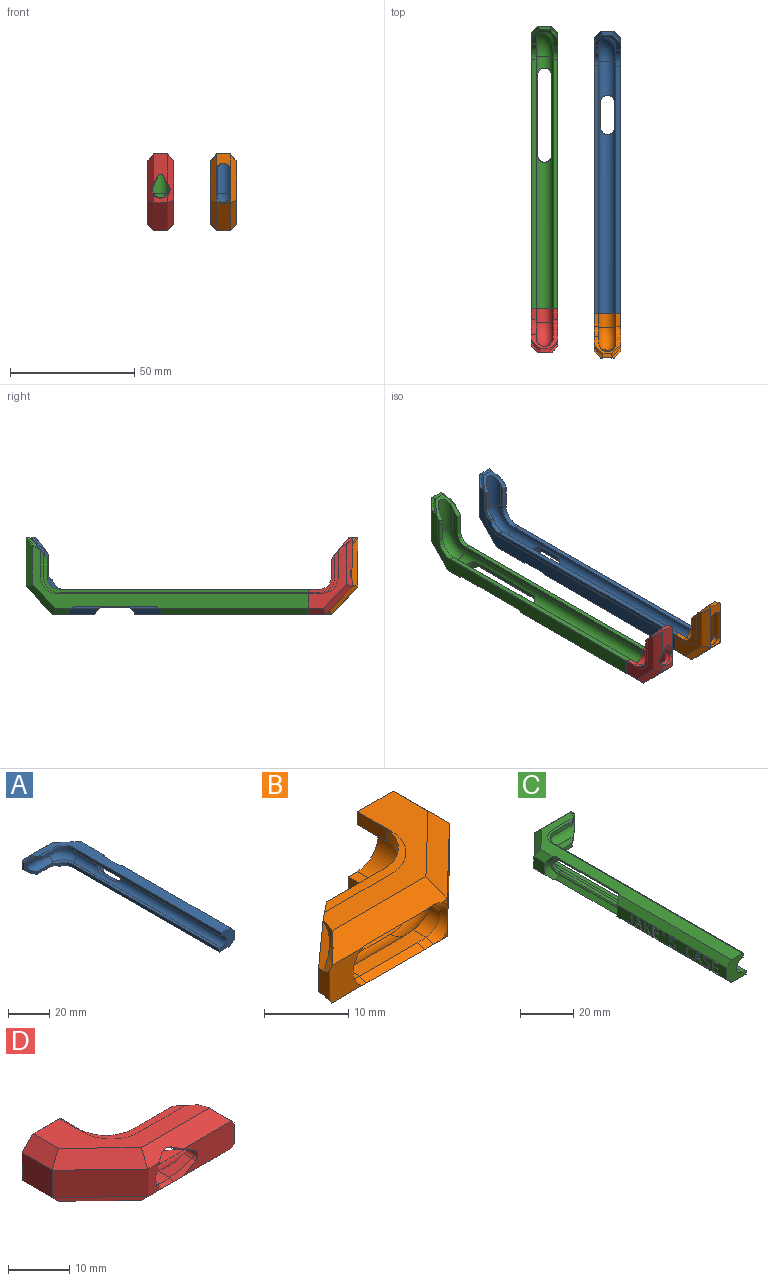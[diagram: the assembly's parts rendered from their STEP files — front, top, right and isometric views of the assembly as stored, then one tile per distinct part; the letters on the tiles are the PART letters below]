
ASSEMBLY  parts=4 mates=2
PART A: 59 faces, bbox 45.8x131.7x47.1 mm
  f0: plane 10.75x7.07mm, normal (-0.63,-0.78,0), area 27.3mm2, adj f1,f5,f6,f7,f8,f9,f15,f27
  f1: plane 107.74x17.21mm, normal (0,0,-1), area 24.9mm2, adj f0,f31,f32,f44,f52,f53,f54,f55
  f2: plane 15.59x6.28mm, normal (1,0,0), area 78.9mm2, adj f3,f19,f22,f23
  f3: plane 11.22x10.82mm, normal (0.69,0.72,0), area 84.7mm2, adj f2,f4,f18,f24
  f4: plane 19.84x5.44mm, normal (0,1,0), area 107.9mm2, adj f3,f7,f16,f17,f25
  f5: cylinder r=0.51mm len=8.54mm, axis (1,0,0), area 7mm2, adj f0,f9,f13,f28
  f6: plane 4.34x3.96mm, normal (-0.56,0,-0.83), area 4.9mm2, adj f0,f7,f26
  f7: plane 5.4x1.58mm, normal (-1,0,0), area 7.5mm2, adj f0,f4,f6,f8,f16,f25,f26
  f8: plane 4.39x4.01mm, normal (-0.56,0,0.83), area 5.1mm2, adj f0,f7,f16
  f9: plane 7.84x1.24mm, normal (0,-1,0), area 9.7mm2, adj f0,f5,f30,f31
  f10: cylinder r=0.51mm len=10.2mm, axis (0,-1,0), area 12.1mm2, adj f12,f14,f21,f33
  f11: cylinder r=0.51mm len=10.2mm, axis (0,-1,0), area 12.3mm2, adj f12,f14,f20,f35
  f12: bspline ~7.32x3.94mm, area 9.9mm2, adj f10,f11,f22,f36
  f13: bspline ~3.96x1.52mm, area 1.8mm2, adj f5,f29,f30,f39
  f14: bspline ~7.32x3.93mm, area 9.9mm2, adj f10,f11,f34,f41
  f15: bspline ~23.11x23.11mm, area 0.1mm2, adj f0,f16,f51
  f16: bspline ~23.11x23.11mm, area 5.8mm2, adj f4,f7,f8,f15,f17,f51
  f17: plane 19.78x2.54mm, normal (0,0.71,0.71), area 63mm2, adj f4,f16,f18,f51
  f18: plane 12.24x11.9mm, normal (0.49,0.51,0.71), area 52.2mm2, adj f3,f17,f19,f51
  f19: plane 16.98x3.13mm, normal (0.71,0,0.71), area 53.1mm2, adj f2,f18,f22,f51
  f20: plane 10.2x1.56mm, normal (0.72,0,-0.7), area 22.1mm2, adj f11,f22,f41,f51
  f21: plane 10.2x1.73mm, normal (0.69,0,0.73), area 24.3mm2, adj f10,f22,f41,f50
  f22: bspline ~16.25x7.94mm, area 45.7mm2, adj f2,f12,f19,f20,f21,f23,f50,f51
  f23: plane 17.36x3.2mm, normal (0.71,0,-0.71), area 53.6mm2, adj f2,f22,f24,f50
  f24: plane 12.24x11.9mm, normal (0.49,0.51,-0.71), area 52.2mm2, adj f3,f23,f25,f50
  f25: plane 19.84x2.54mm, normal (0,0.71,-0.71), area 63.3mm2, adj f4,f7,f24,f26,f50
  f26: bspline ~23.11x23.11mm, area 5.3mm2, adj f6,f7,f25,f27,f50
  f27: bspline ~23.11x23.11mm, area 0mm2, adj f0,f26,f28,f50
  f28: plane 8.54x0.06mm, normal (0,-0.99,-0.12), area 0.5mm2, adj f5,f27,f29,f50
  f29: bspline ~6.39x2.18mm, area 0.1mm2, adj f13,f28,f38,f50
  f30: cylinder r=4.1mm len=3.88mm, axis (0,0,1), area 6.4mm2, adj f9,f13,f31,f39,f40,f45
  f31: cylinder r=3.43mm len=15.1mm, axis (1,0,0), area 145.4mm2, adj f0,f1,f9,f30,f32,f45
  f32: torus R=6.37mm, axis (0,0,-1), area 144.5mm2, adj f1,f31,f44,f45
  f33: plane 10.2x1.33mm, normal (0,0,1), area 13.6mm2, adj f10,f34,f36,f44
  f34: cylinder r=2.79mm len=5.59mm, axis (-1,0,0), area 11.4mm2, adj f14,f33,f35,f44
  f35: plane 10.2x1.39mm, normal (0,0,-1), area 14.2mm2, adj f11,f34,f36,f44
  f36: cylinder r=2.79mm len=5.59mm, axis (-1,0,0), area 11.4mm2, adj f12,f33,f35,f44
  f37: cylinder r=6.37mm len=6.37mm, axis (0,0,-1), area 0.2mm2, adj f38,f43,f46,f50
  f38: plane 0.87x0.02mm, normal (0,-1,0), area 0mm2, adj f29,f37,f43,f50
  f39: torus R=4.61mm, axis (0,0,-1), area 2.7mm2, adj f13,f30,f40,f43
  f40: cylinder r=4.77mm len=5.29mm, axis (0,0,1), area 12.9mm2, adj f30,f39,f42,f43,f45
  f41: bspline ~16.25x7.94mm, area 45.7mm2, adj f14,f20,f21,f47,f48,f49,f50,f51
  f42: plane 99.7x1.78mm, normal (-1,0,0), area 177.3mm2, adj f40,f43,f45,f52
  f43: plane 107.74x7.25mm, normal (0,0,-1), area 174.7mm2, adj f37,f38,f39,f40,f42,f46,f52
  f44: cylinder r=3.43mm len=101.37mm, axis (0,-1,0), area 1024mm2, adj f1,f32,f33,f34,f35,f36,f45,f52
  f45: plane 107.74x8.86mm, normal (0,0,1), area 176.7mm2, adj f30,f31,f32,f40,f42,f44,f52
  f46: plane 101.37x0.02mm, normal (-1,0,0), area 2.1mm2, adj f37,f43,f50,f52
  f47: plane 74.13x3.14mm, normal (0.71,0,0.71), area 260.3mm2, adj f41,f49,f51,f52
  f48: plane 74.51x3.2mm, normal (0.71,0,-0.71), area 260.8mm2, adj f41,f49,f50,f52
  f49: plane 72.74x6.29mm, normal (1,0,0), area 389.6mm2, adj f41,f47,f48,f52
  f50: plane 111.22x25.47mm, normal (0,0,-1), area 681.3mm2, adj f21,f22,f23,f24,f25,f26,f27,f28
  f51: plane 111.34x25.52mm, normal (0,0,1), area 682.3mm2, adj f15,f16,f17,f18,f19,f20,f22,f41
  f52: plane 10.52x10.11mm, normal (0,-1,0), area 68mm2, adj f1,f42,f43,f44,f45,f46,f47,f48
  f53: plane 99.61x1.87mm, normal (-1,0,0), area 186mm2, adj f1,f52,f55,f57,f58
  f54: plane 6.88x1.88mm, normal (0,-1,0), area 12.8mm2, adj f1,f55,f56,f58
  f55: cylinder r=6.27mm len=6.94mm, axis (0,0,1), area 20.9mm2, adj f1,f53,f54,f58
  f56: plane 1.89x1.88mm, normal (0,-1,0), area 3.5mm2, adj f0,f1,f54,f58
  f57: bspline ~0.09x0.04mm, area 0mm2, adj f52,f53,f58
  f58: plane 107.74x17.22mm, normal (0,0,1), area 25mm2, adj f0,f51,f53,f54,f55,f56,f57
PART B: 51 faces, bbox 39.8x36x47.2 mm
  f0: plane 17.45x11.89mm, normal (0,0,-1), area 22.2mm2, adj f13,f16,f17,f18,f44,f45,f46,f47
  f1: plane 25.55x15.24mm, normal (0,0,1), area 116.6mm2, adj f33,f35,f39,f40,f43,f44,f50
  f2: plane 5.7x5.46mm, normal (0,-1,0), area 24.1mm2, adj f7,f12,f34,f35,f42,f43
  f3: plane 1.07x0.98mm, normal (0,-1,0), area 0.4mm2, adj f5,f31,f43
  f4: plane 25.54x15.19mm, normal (0,0,-1), area 116.7mm2, adj f7,f8,f9,f10,f11,f37,f38,f42
  f5: plane 12.21x11.81mm, normal (0.69,-0.72,0), area 83.4mm2, adj f3,f31,f36,f38,f40,f41
  f6: plane 9.77x1.02mm, normal (0,-0.45,0.89), area 11.2mm2, adj f21,f32,f34,f42
  f7: bspline ~23.11x23.11mm, area 5.6mm2, adj f2,f4,f8,f12,f27,f42
  f8: bspline ~23.11x23.11mm, area 0.1mm2, adj f4,f7,f9,f13
  f9: plane 11.08x0.02mm, normal (0,1,0), area 0.2mm2, adj f4,f8,f10,f19
  f10: cylinder r=6.37mm len=6.37mm, axis (0,0,-1), area 0.2mm2, adj f4,f9,f11,f19
  f11: plane 5.52x0.02mm, normal (-1,0,0), area 0.1mm2, adj f4,f10,f19,f44
  f12: plane 4.13x1.79mm, normal (-1,0,0), area 6.5mm2, adj f2,f7,f13,f27,f28,f35
  f13: plane 10.5x8.54mm, normal (-0.63,0.78,0), area 32.4mm2, adj f0,f8,f12,f15,f16,f19,f24,f27
  f14: cylinder r=4.73mm len=1.78mm, axis (0,0,-1), area 1.5mm2, adj f15,f19,f24,f25
  f15: plane 17.45x11.89mm, normal (0,0,1), area 54.1mm2, adj f13,f14,f16,f17,f18,f24,f25,f26
  f16: cylinder r=3.43mm len=15.36mm, axis (-1,0,0), area 89.5mm2, adj f0,f13,f15,f17,f20,f21,f23
  f17: torus R=6.37mm, axis (0,0,-1), area 127.5mm2, adj f0,f15,f16,f18,f21,f22,f23
  f18: cylinder r=3.43mm len=6.85mm, axis (0,-1,0), area 59.4mm2, adj f0,f15,f17,f44
  f19: plane 17.45x11.89mm, normal (0,0,-1), area 54.1mm2, adj f9,f10,f11,f13,f14,f24,f25,f26
  f20: cylinder r=2.32mm len=4.65mm, axis (0,1,0), area 15.6mm2, adj f16,f21,f23,f34
  f21: plane 11.25x2.27mm, normal (0,0,1), area 24.1mm2, adj f6,f16,f17,f20,f22,f32
  f22: cylinder r=2.32mm len=4.65mm, axis (0,1,0), area 15.8mm2, adj f17,f21,f23,f31
  f23: plane 11.25x2.26mm, normal (0,0,-1), area 24.1mm2, adj f16,f17,f20,f22,f29,f30
  f24: plane 7.58x1.78mm, normal (0,1,0), area 13.5mm2, adj f13,f14,f15,f19
  f25: cylinder r=4.79mm len=4.14mm, axis (0,0,1), area 11mm2, adj f14,f15,f19,f26
  f26: plane 4.87x1.78mm, normal (-1,0,0), area 8.7mm2, adj f15,f19,f25,f44
  f27: plane 3.88x3.76mm, normal (-0.67,0,-0.75), area 5.7mm2, adj f7,f12,f13
  f28: plane 3.9x3.79mm, normal (-0.67,0,0.75), area 5.8mm2, adj f12,f13,f35
  f29: plane 9.77x1.07mm, normal (0,-0.45,-0.9), area 11.7mm2, adj f23,f30,f34,f43
  f30: cone r=11.03mm half-angle=63.5deg, axis (0,0,1), area 1.9mm2, adj f23,f29,f31,f43
  f31: bspline ~10.32x6.08mm, area 11.6mm2, adj f3,f5,f22,f30,f32,f41,f42,f43
  f32: cone r=11.02mm half-angle=63.4deg, axis (0,0,-1), area 1.8mm2, adj f6,f21,f31,f42
  f33: bspline ~23.11x23.11mm, area 0.2mm2, adj f1,f13,f35
  f34: bspline ~10.32x6.9mm, area 7.2mm2, adj f2,f6,f20,f29,f42,f43
  f35: bspline ~23.11x23.11mm, area 6mm2, adj f1,f2,f12,f28,f33,f43
  f36: plane 6.91x5.44mm, normal (1,0,0), area 37.5mm2, adj f5,f37,f39,f44
  f37: plane 6.91x2.54mm, normal (0.71,0,-0.71), area 22.9mm2, adj f4,f36,f38,f44
  f38: plane 12.24x11.9mm, normal (0.49,-0.51,-0.71), area 52.2mm2, adj f4,f5,f37,f42
  f39: plane 6.91x2.54mm, normal (0.71,0,0.71), area 22.9mm2, adj f1,f36,f40,f44
  f40: plane 12.24x11.9mm, normal (0.49,-0.51,0.71), area 52.2mm2, adj f1,f5,f39,f43
  f41: plane 0.9x0.89mm, normal (0,-1,0), area 0.3mm2, adj f5,f31,f42
  f42: plane 19.45x2.62mm, normal (0,-0.71,-0.71), area 60mm2, adj f2,f4,f6,f7,f31,f32,f34,f38
  f43: plane 19.35x2.61mm, normal (0,-0.71,0.71), area 60.8mm2, adj f1,f2,f3,f29,f30,f31,f34,f35
  f44: plane 10.52x10.11mm, normal (0,1,0), area 68mm2, adj f0,f1,f4,f11,f15,f18,f19,f26
  f45: plane 6.93x1.87mm, normal (0,1,0), area 12.9mm2, adj f0,f46,f48,f50
  f46: cylinder r=6.29mm len=6.93mm, axis (0,0,1), area 18.5mm2, adj f0,f45,f47,f50
  f47: plane 4.96x1.87mm, normal (-1,0,0), area 9.3mm2, adj f0,f44,f46,f49,f50
  f48: plane 1.87x1.87mm, normal (0,1,0), area 3.5mm2, adj f0,f13,f45,f50
  f49: bspline ~0.09x0.04mm, area 0mm2, adj f44,f47,f50
  f50: plane 17.45x11.9mm, normal (0,0,1), area 22.2mm2, adj f1,f13,f45,f46,f47,f48,f49
PART C: 203 faces, bbox 45.8x131.7x47.1 mm
  f0: plane 107.74x17.21mm, normal (0,0,-1), area 41.8mm2, adj f1,f2,f9,f28,f37,f197,f198,f199
  f1: plane 10.5x8.65mm, normal (0.63,-0.78,0), area 35.3mm2, adj f0,f7,f8,f24,f26,f28,f39,f41
  f2: plane 10.52x10.21mm, normal (0,-1,0), area 68.5mm2, adj f0,f3,f4,f5,f6,f7,f8,f9
  f3: plane 11.84x5.47mm, normal (-1,0,0), area 47.1mm2, adj f2,f4,f5,f64,f65,f66,f67,f68
  f4: plane 61.01x3.15mm, normal (-0.71,0,0.71), area 212.9mm2, adj f2,f3,f6,f13,f14,f15,f22,f54
  f5: plane 61.1x3.18mm, normal (-0.71,0,-0.71), area 212.6mm2, adj f2,f3,f12,f13,f14,f15,f16,f17
  f6: plane 111.3x25.48mm, normal (0,0,1), area 667mm2, adj f2,f4,f19,f21,f22,f23,f24,f48
  f7: plane 107.74x17.21mm, normal (0,0,-1), area 209.3mm2, adj f1,f2,f10,f11,f38,f39,f40,f44
  f8: plane 107.74x17.21mm, normal (0,0,1), area 209.3mm2, adj f1,f2,f9,f10,f28,f37,f38,f39
  f9: cylinder r=3.43mm len=101.37mm, axis (0,1,0), area 879.2mm2, adj f0,f2,f8,f29,f30,f31,f32,f37
  f10: plane 100.21x1.78mm, normal (1,0,0), area 178.2mm2, adj f2,f7,f8,f38
  f11: plane 101.37x0.02mm, normal (1,0,0), area 2.1mm2, adj f2,f7,f12,f45
  f12: plane 111.27x25.52mm, normal (0,0,-1), area 670.3mm2, adj f2,f5,f11,f21,f22,f27,f43,f44
  f13: plane 11.2x5.47mm, normal (-1,0,0), area 33.3mm2, adj f4,f5,f54,f55,f56,f57,f58,f59
  f14: plane 31.59x6.32mm, normal (-1,0,0), area 117.6mm2, adj f4,f5,f22,f90,f91,f92,f93,f94
  f15: plane 10.36x5.51mm, normal (-1,0,0), area 38mm2, adj f4,f5,f85,f86,f87,f88,f100,f101
  f16: plane 2.88x1.67mm, normal (-1,0,0), area 3.9mm2, adj f5,f185,f191,f192
  f17: plane 2.88x1.67mm, normal (-1,0,0), area 3.9mm2, adj f5,f171,f177,f178
  f18: plane 2.57x2.17mm, normal (-1,0,0), area 3.4mm2, adj f5,f153,f164,f165
  f19: bspline ~23.11x23.11mm, area 5.8mm2, adj f6,f24,f26,f42,f47,f50
  f20: plane 11.22x10.82mm, normal (-0.69,0.72,0), area 84.7mm2, adj f25,f47,f49,f52
  f21: bspline ~16.27x7.89mm, area 45.8mm2, adj f6,f12,f23,f25,f34,f46,f48,f51
  f22: bspline ~16.27x7.89mm, area 45.8mm2, adj f4,f5,f6,f12,f14,f23,f36,f46
  f23: plane 32.32x1.6mm, normal (-0.71,0,-0.7), area 73mm2, adj f6,f21,f22,f33
  f24: bspline ~23.11x23.11mm, area 0.1mm2, adj f1,f6,f19
  f25: plane 6.68x6.28mm, normal (-1,0,0), area 30.6mm2, adj f20,f21,f48,f51
  f26: plane 5.4x1.58mm, normal (1,0,0), area 7.5mm2, adj f1,f19,f27,f41,f42,f47,f53
  f27: bspline ~23.11x23.11mm, area 5.3mm2, adj f12,f26,f41,f43,f53
  f28: cylinder r=3.43mm len=15.1mm, axis (1,0,0), area 145.7mm2, adj f0,f1,f8,f37
  f29: cylinder r=2.8mm len=5.59mm, axis (1,0,0), area 11.4mm2, adj f9,f30,f32,f34
  f30: plane 32.32x1.37mm, normal (0,0,-1), area 44.2mm2, adj f9,f29,f31,f33
  f31: cylinder r=2.8mm len=5.59mm, axis (1,0,0), area 11.4mm2, adj f9,f30,f32,f36
  f32: plane 32.32x1.35mm, normal (0,0,1), area 43.6mm2, adj f9,f29,f31,f35
  f33: cylinder r=0.51mm len=32.32mm, axis (0,1,0), area 38.7mm2, adj f23,f30,f34,f36
  f34: bspline ~7.33x3.93mm, area 9.9mm2, adj f21,f29,f33,f35
  f35: cylinder r=0.51mm len=32.32mm, axis (0,1,0), area 38.5mm2, adj f32,f34,f36,f46
  f36: bspline ~7.33x3.94mm, area 9.9mm2, adj f22,f31,f33,f35
  f37: torus R=6.37mm, axis (0,0,-1), area 144.5mm2, adj f0,f8,f9,f28
  f38: cylinder r=4.76mm len=4.13mm, axis (0,0,-1), area 8.9mm2, adj f7,f8,f10,f40
  f39: plane 7.39x1.78mm, normal (0,-1,0), area 13.1mm2, adj f1,f7,f8,f40
  f40: cylinder r=4.73mm len=2.44mm, axis (0,0,1), area 4.6mm2, adj f7,f8,f38,f39
  f41: plane 4.34x3.96mm, normal (0.56,0,-0.83), area 4.9mm2, adj f1,f26,f27
  f42: plane 4.39x4.01mm, normal (0.56,0,0.83), area 5.1mm2, adj f1,f19,f26
  f43: bspline ~23.11x23.11mm, area 0mm2, adj f1,f12,f27,f44
  f44: plane 10.84x0.02mm, normal (0,-1,0), area 0.2mm2, adj f7,f12,f43,f45
  f45: cylinder r=6.37mm len=6.37mm, axis (0,0,-1), area 0.2mm2, adj f7,f11,f12,f44
  f46: plane 32.32x1.63mm, normal (-0.7,0,0.72), area 73.5mm2, adj f12,f21,f22,f35
  f47: plane 19.84x5.44mm, normal (0,1,0), area 107.9mm2, adj f19,f20,f26,f50,f53
  f48: plane 8.23x3.16mm, normal (-0.71,0,0.71), area 21.4mm2, adj f6,f21,f25,f49
  f49: plane 12.24x11.9mm, normal (-0.49,0.51,0.71), area 52.2mm2, adj f6,f20,f48,f50
  f50: plane 19.78x2.54mm, normal (0,0.71,0.71), area 63mm2, adj f6,f19,f47,f49
  f51: plane 8.31x3.17mm, normal (-0.71,0,-0.71), area 21.5mm2, adj f12,f21,f25,f52
  f52: plane 12.24x11.9mm, normal (-0.49,0.51,-0.71), area 52.2mm2, adj f12,f20,f51,f53
  f53: plane 19.84x2.54mm, normal (0,0.71,-0.71), area 63.3mm2, adj f12,f26,f27,f47,f52
  f54: extruded ~1.3x0.76mm, area 1mm2, adj f4,f13,f55,f73,f74
  f55: extruded ~1x0.76mm, area 0.9mm2, adj f13,f54,f56,f74
  f56: extruded ~0.97x0.76mm, area 0.8mm2, adj f13,f55,f57,f74
  f57: extruded ~1.1x0.76mm, area 1mm2, adj f13,f56,f58,f74
  f58: extruded ~1.05x0.76mm, area 0.9mm2, adj f13,f57,f59,f74
  f59: extruded ~0.76x0.59mm, area 0.5mm2, adj f13,f58,f60,f74
  f60: extruded ~1.29x0.89mm, area 1.4mm2, adj f13,f59,f61,f74
  f61: extruded ~1.53x0.76mm, area 1.2mm2, adj f13,f60,f62,f74
  f62: plane 0.76x0.66mm, normal (0,-1,0), area 0.5mm2, adj f13,f61,f63,f74
  f63: extruded ~1.53x0.76mm, area 1.2mm2, adj f5,f13,f62,f64,f74
  f64: extruded ~1.45x0.76mm, area 1.1mm2, adj f3,f5,f63,f65,f74
  f65: extruded ~1.11x0.76mm, area 1mm2, adj f3,f64,f66,f74
  f66: extruded ~0.89x0.76mm, area 0.7mm2, adj f3,f65,f67,f74
  f67: extruded ~1.21x0.76mm, area 1.1mm2, adj f3,f66,f68,f74
  f68: extruded ~1x0.76mm, area 0.9mm2, adj f3,f67,f69,f74
  f69: extruded ~0.76x0.6mm, area 0.5mm2, adj f3,f68,f70,f74
  f70: extruded ~1.08x0.77mm, area 1.2mm2, adj f3,f69,f71,f74
  f71: extruded ~1.33x0.76mm, area 1mm2, adj f3,f70,f72,f74
  f72: plane 0.76x0.61mm, normal (0,0.93,0.36), area 0.5mm2, adj f3,f71,f73,f74
  f73: extruded ~1.53x0.76mm, area 1.2mm2, adj f3,f4,f54,f72,f74
  f74: plane 5.54x3.49mm, normal (-1,0,0), area 7.3mm2, adj f54,f55,f56,f57,f58,f59,f60,f61
  f75: extruded ~1.32x0.76mm, area 1mm2, adj f5,f13,f76,f88,f89
  f76: plane 0.76x0.6mm, normal (0,1,0), area 0.5mm2, adj f13,f75,f77,f89
  f77: extruded ~1.21x0.76mm, area 0.9mm2, adj f13,f76,f78,f89
  f78: extruded ~1.29x0.76mm, area 1.1mm2, adj f13,f77,f79,f89
  f79: extruded ~1.61x0.76mm, area 1.3mm2, adj f13,f78,f80,f89
  f80: extruded ~1.58x0.76mm, area 1.3mm2, adj f13,f79,f81,f89
  f81: extruded ~1.27x0.76mm, area 1.1mm2, adj f13,f80,f82,f89
  f82: extruded ~1.12x0.76mm, area 0.9mm2, adj f13,f81,f83,f89
  f83: plane 0.76x0.58mm, normal (0,0.89,0.45), area 0.5mm2, adj f13,f82,f84,f89
  f84: extruded ~1.41x0.76mm, area 1.1mm2, adj f4,f13,f83,f85,f89
  f85: extruded ~1.8x0.76mm, area 1.5mm2, adj f4,f15,f84,f86,f89
  f86: extruded ~2.02x0.76mm, area 1.7mm2, adj f15,f85,f87,f89
  f87: extruded ~2.05x0.76mm, area 1.7mm2, adj f15,f86,f88,f89
  f88: extruded ~1.74x0.76mm, area 1.5mm2, adj f5,f15,f75,f87,f89
  f89: plane 5.54x3.88mm, normal (-1,0,0), area 6.6mm2, adj f75,f76,f77,f78,f79,f80,f81,f82
  f90: extruded ~1.3x0.76mm, area 1mm2, adj f4,f14,f91,f109,f110
  f91: extruded ~1x0.76mm, area 0.9mm2, adj f14,f90,f92,f110
  f92: extruded ~0.97x0.76mm, area 0.8mm2, adj f14,f91,f93,f110
  f93: extruded ~1.1x0.76mm, area 1mm2, adj f14,f92,f94,f110
  f94: extruded ~1.05x0.76mm, area 0.9mm2, adj f14,f93,f95,f110
  f95: extruded ~0.76x0.59mm, area 0.5mm2, adj f14,f94,f96,f110
  f96: extruded ~1.29x0.89mm, area 1.4mm2, adj f14,f95,f97,f110
  f97: extruded ~1.53x0.76mm, area 1.2mm2, adj f14,f96,f98,f110
  f98: plane 0.76x0.66mm, normal (0,-1,0), area 0.5mm2, adj f14,f97,f99,f110
  f99: extruded ~1.53x0.76mm, area 1.2mm2, adj f5,f14,f98,f100,f110
  f100: extruded ~1.45x0.76mm, area 1.1mm2, adj f5,f15,f99,f101,f110
  f101: extruded ~1.11x0.76mm, area 1mm2, adj f15,f100,f102,f110
  f102: extruded ~0.89x0.76mm, area 0.7mm2, adj f15,f101,f103,f110
  f103: extruded ~1.21x0.76mm, area 1.1mm2, adj f15,f102,f104,f110
  f104: extruded ~1x0.76mm, area 0.9mm2, adj f15,f103,f105,f110
  f105: extruded ~0.76x0.6mm, area 0.5mm2, adj f15,f104,f106,f110
  f106: extruded ~1.08x0.77mm, area 1.2mm2, adj f15,f105,f107,f110
  f107: extruded ~1.33x0.76mm, area 1mm2, adj f15,f106,f108,f110
  f108: plane 0.76x0.61mm, normal (0,0.93,0.36), area 0.5mm2, adj f15,f107,f109,f110
  f109: extruded ~1.53x0.76mm, area 1.2mm2, adj f4,f15,f90,f108,f110
  f110: plane 5.54x3.49mm, normal (-1,0,0), area 7.3mm2, adj f90,f91,f92,f93,f94,f95,f96,f97
  f111: extruded ~1.39x0.76mm, area 1.1mm2, adj f5,f14,f112,f120,f121
  f112: extruded ~1.27x0.76mm, area 1.1mm2, adj f14,f111,f113,f121
  f113: plane 3.73x0.76mm, normal (0,1,0), area 2.8mm2, adj f14,f112,f114,f121
  f114: plane 0.76x0.69mm, normal (0,0,-1), area 0.5mm2, adj f14,f113,f115,f121
  f115: plane 3.74x0.76mm, normal (0,-1,0), area 2.8mm2, adj f14,f114,f116,f121
  f116: extruded ~0.83x0.76mm, area 0.7mm2, adj f14,f115,f117,f121
  f117: extruded ~0.94x0.76mm, area 0.8mm2, adj f14,f116,f118,f121
  f118: extruded ~1.14x0.76mm, area 0.9mm2, adj f14,f117,f119,f121
  f119: plane 0.76x0.61mm, normal (0,-1,0), area 0.5mm2, adj f14,f118,f120,f121
  f120: extruded ~1.2x0.76mm, area 0.9mm2, adj f5,f14,f111,f119,f121
  f121: plane 5.47x3.1mm, normal (-1,0,0), area 4.9mm2, adj f111,f112,f113,f114,f115,f116,f117,f118
  f122: plane 5.39x0.76mm, normal (0,-1,0), area 4.1mm2, adj f14,f123,f133,f134
  f123: plane 3.1x0.76mm, normal (0,0,1), area 2.4mm2, adj f5,f122,f124,f134
  f124: plane 0.76x0.61mm, normal (0,1,0), area 0.5mm2, adj f14,f123,f125,f134
  f125: plane 2.42x0.76mm, normal (0,0,-1), area 1.8mm2, adj f14,f124,f126,f134
  f126: plane 1.92x0.76mm, normal (0,1,0), area 1.5mm2, adj f14,f125,f127,f134
  f127: plane 2.28x0.76mm, normal (0,0,1), area 1.7mm2, adj f14,f126,f128,f134
  f128: plane 0.76x0.6mm, normal (0,1,0), area 0.5mm2, adj f14,f127,f129,f134
  f129: plane 2.28x0.76mm, normal (0,0,-1), area 1.7mm2, adj f14,f128,f130,f134
  f130: plane 1.67x0.76mm, normal (0,1,0), area 1.3mm2, adj f14,f129,f131,f134
  f131: plane 2.42x0.76mm, normal (0,0,1), area 1.8mm2, adj f14,f130,f132,f134
  f132: plane 0.76x0.61mm, normal (0,1,0), area 0.5mm2, adj f14,f131,f133,f134
  f133: plane 3.1x0.76mm, normal (0,0,-1), area 2.4mm2, adj f14,f122,f132,f134
  f134: plane 5.39x3.1mm, normal (-1,0,0), area 8mm2, adj f122,f123,f124,f125,f126,f127,f128,f129
  f135: plane 1.95x0.76mm, normal (0,1,0.08), area 1.5mm2, adj f14,f136,f138,f139
  f136: plane 0.87x0.76mm, normal (0,0,-1), area 0.7mm2, adj f14,f135,f137,f139
  f137: plane 1.95x0.76mm, normal (0,-1,0.08), area 1.5mm2, adj f14,f136,f138,f139
  f138: plane 0.76x0.57mm, normal (0,0,1), area 0.4mm2, adj f14,f135,f137,f139
  f139: plane 1.95x0.87mm, normal (-1,0,0), area 1.4mm2, adj f135,f136,f137,f138
  f140: plane 5.39x0.76mm, normal (0,-1,0), area 4.1mm2, adj f3,f141,f151,f152
  f141: plane 3.1x0.76mm, normal (0,0,1), area 2.4mm2, adj f5,f140,f142,f152
  f142: plane 0.76x0.61mm, normal (0,1,0), area 0.5mm2, adj f3,f141,f143,f152
  f143: plane 2.42x0.76mm, normal (0,0,-1), area 1.8mm2, adj f3,f142,f144,f152
  f144: plane 1.92x0.76mm, normal (0,1,0), area 1.5mm2, adj f3,f143,f145,f152
  f145: plane 2.28x0.76mm, normal (0,0,1), area 1.7mm2, adj f3,f144,f146,f152
  f146: plane 0.76x0.6mm, normal (0,1,0), area 0.5mm2, adj f3,f145,f147,f152
  f147: plane 2.28x0.76mm, normal (0,0,-1), area 1.7mm2, adj f3,f146,f148,f152
  f148: plane 1.67x0.76mm, normal (0,1,0), area 1.3mm2, adj f3,f147,f149,f152
  f149: plane 2.42x0.76mm, normal (0,0,1), area 1.8mm2, adj f3,f148,f150,f152
  f150: plane 0.76x0.61mm, normal (0,1,0), area 0.5mm2, adj f3,f149,f151,f152
  f151: plane 3.1x0.76mm, normal (0,0,-1), area 2.4mm2, adj f3,f140,f150,f152
  f152: plane 5.39x3.1mm, normal (-1,0,0), area 8mm2, adj f140,f141,f142,f143,f144,f145,f146,f147
  f153: plane 2.57x1.66mm, normal (0,-0.84,0.54), area 2.3mm2, adj f18,f154,f165,f166
  f154: plane 0.78x0.76mm, normal (0,0,1), area 0.6mm2, adj f5,f153,f155,f166
  f155: plane 3.04x1.99mm, normal (0,0.84,-0.55), area 2.8mm2, adj f14,f154,f156,f166
  f156: plane 2.35x1.92mm, normal (0,0.77,0.63), area 2.3mm2, adj f14,f155,f157,f166
  f157: plane 0.77x0.76mm, normal (0,0,-1), area 0.6mm2, adj f14,f156,f158,f166
  f158: plane 2.08x1.67mm, normal (0,-0.78,-0.63), area 2mm2, adj f14,f157,f159,f166
  f159: plane 0.76x0.62mm, normal (0,-0.81,-0.58), area 0.6mm2, adj f14,f158,f160,f166
  f160: plane 2.7x0.76mm, normal (0,1,0), area 2.1mm2, adj f14,f159,f161,f166
  f161: plane 0.76x0.69mm, normal (0,0,-1), area 0.5mm2, adj f14,f160,f162,f166
  f162: plane 5.39x0.76mm, normal (0,-1,0), area 4.1mm2, adj f14,f161,f163,f166
  f163: plane 0.76x0.69mm, normal (0,0,1), area 0.5mm2, adj f5,f162,f164,f166
  f164: plane 2.15x0.76mm, normal (0,1,0), area 1.6mm2, adj f18,f163,f165,f166
  f165: plane 0.76x0.52mm, normal (0,0.63,0.78), area 0.5mm2, adj f18,f153,f164,f166
  f166: plane 5.39x3.64mm, normal (-1,0,0), area 8mm2, adj f153,f154,f155,f156,f157,f158,f159,f160
  f167: plane 1.56x0.76mm, normal (0,-0.95,0.3), area 1.2mm2, adj f168,f179,f180,f195
  f168: plane 1.42x0.76mm, normal (0,0,-1), area 1.1mm2, adj f167,f169,f180,f195
  f169: plane 1.72x0.76mm, normal (0,0.96,0.29), area 1.4mm2, adj f168,f170,f180,f195
  f170: extruded ~0.76x0.68mm, area 0.5mm2, adj f169,f179,f180,f195
  f171: plane 1.67x0.76mm, normal (0,-0.95,0.3), area 1.3mm2, adj f17,f172,f178,f180
  f172: plane 0.76x0.71mm, normal (0,0,1), area 0.5mm2, adj f5,f171,f173,f180
  f173: plane 5.41x1.79mm, normal (0,0.95,-0.31), area 4.3mm2, adj f14,f172,f174,f180
  f174: plane 0.76x0.72mm, normal (0,0,-1), area 0.5mm2, adj f14,f173,f175,f180
  f175: plane 5.41x1.78mm, normal (0,-0.95,-0.31), area 4.3mm2, adj f14,f174,f176,f180
  f176: plane 0.76x0.7mm, normal (0,0,1), area 0.5mm2, adj f5,f175,f177,f180
  f177: plane 1.67x0.76mm, normal (0,0.95,0.31), area 1.3mm2, adj f17,f176,f178,f180
  f178: plane 1.81x0.76mm, normal (0,0,1), area 1.4mm2, adj f17,f171,f177,f180
  f179: extruded ~0.83x0.76mm, area 0.7mm2, adj f167,f170,f180,f195
  f180: plane 5.41x4.29mm, normal (-1,0,0), area 8mm2, adj f167,f168,f169,f170,f171,f172,f173,f174
  f181: plane 1.56x0.76mm, normal (0,-0.95,0.3), area 1.2mm2, adj f182,f193,f194,f196
  f182: plane 1.42x0.76mm, normal (0,0,-1), area 1.1mm2, adj f181,f183,f194,f196
  f183: plane 1.72x0.76mm, normal (0,0.96,0.29), area 1.4mm2, adj f182,f184,f194,f196
  f184: extruded ~0.76x0.68mm, area 0.5mm2, adj f183,f193,f194,f196
  f185: plane 1.67x0.76mm, normal (0,-0.95,0.3), area 1.3mm2, adj f16,f186,f192,f194
  f186: plane 0.76x0.71mm, normal (0,0,1), area 0.5mm2, adj f5,f185,f187,f194
  f187: plane 5.41x1.79mm, normal (0,0.95,-0.31), area 4.3mm2, adj f13,f186,f188,f194
  f188: plane 0.76x0.72mm, normal (0,0,-1), area 0.5mm2, adj f13,f187,f189,f194
  f189: plane 5.41x1.78mm, normal (0,-0.95,-0.31), area 4.3mm2, adj f13,f188,f190,f194
  f190: plane 0.76x0.7mm, normal (0,0,1), area 0.5mm2, adj f5,f189,f191,f194
  f191: plane 1.67x0.76mm, normal (0,0.95,0.31), area 1.3mm2, adj f16,f190,f192,f194
  f192: plane 1.81x0.76mm, normal (0,0,1), area 1.4mm2, adj f16,f185,f191,f194
  f193: extruded ~0.83x0.76mm, area 0.7mm2, adj f181,f184,f194,f196
  f194: plane 5.41x4.29mm, normal (-1,0,0), area 8mm2, adj f181,f182,f183,f184,f185,f186,f187,f188
  f195: plane 2.4x1.42mm, normal (-1,0,0), area 1.6mm2, adj f167,f168,f169,f170,f179
  f196: plane 2.4x1.42mm, normal (-1,0,0), area 1.6mm2, adj f181,f182,f183,f184,f193
  f197: plane 7.4x1.88mm, normal (0,-1,0), area 13.8mm2, adj f0,f199,f200,f202
  f198: plane 100.29x1.87mm, normal (1,0,0), area 187.2mm2, adj f0,f2,f199,f201,f202
  f199: cylinder r=6.23mm len=6.23mm, axis (0,0,1), area 18.3mm2, adj f0,f197,f198,f202
  f200: plane 1.89x1.88mm, normal (0,-1,0), area 3.5mm2, adj f0,f1,f197,f202
  f201: bspline ~0.2x0.09mm, area 0mm2, adj f2,f198,f202
  f202: plane 107.74x17.22mm, normal (0,0,1), area 41.8mm2, adj f1,f6,f197,f198,f199,f200,f201
PART D: 49 faces, bbox 39.5x35.6x46.8 mm
  f0: plane 17.17x11.89mm, normal (0,0,-1), area 23.9mm2, adj f1,f23,f24,f25,f36,f43,f44,f45
  f1: plane 10.52x10.21mm, normal (0,1,0), area 68.5mm2, adj f0,f33,f34,f35,f36,f37,f38,f39
  f2: bspline ~6.43x4.01mm, area 1.7mm2, adj f3,f7,f13,f16
  f3: bspline ~4.25x2.73mm, area 5mm2, adj f2,f4,f6,f16,f19
  f4: bspline ~5.56x4.33mm, area 3mm2, adj f3,f9,f11,f19
  f5: plane 3.71x3.61mm, normal (0.67,0,0.75), area 4.5mm2, adj f14,f18,f23
  f6: plane 4.87x3.97mm, normal (-0.43,0,-0.9), area 9.7mm2, adj f3,f7,f9,f24
  f7: cylinder r=1mm len=1.82mm, axis (0,1,0), area 4.1mm2, adj f2,f6,f8,f24
  f8: plane 4.88x3.99mm, normal (-0.43,0,0.9), area 9.7mm2, adj f7,f9,f13,f24
  f9: cylinder r=3.25mm len=6.5mm, axis (0,1,0), area 26.1mm2, adj f4,f6,f8,f11,f12,f24,f25
  f10: plane 5.44x2.76mm, normal (0,-1,0), area 11.7mm2, adj f11,f19,f20,f28
  f11: bspline ~12.79x7.02mm, area 7.8mm2, adj f4,f9,f10,f12,f19,f28
  f12: bspline ~5.56x4.35mm, area 2.9mm2, adj f9,f11,f13,f28
  f13: bspline ~4.25x2.72mm, area 4.9mm2, adj f2,f8,f12,f16,f28
  f14: plane 4.13x1.52mm, normal (1,0,0), area 5.6mm2, adj f5,f15,f16,f18,f23,f29
  f15: plane 3.68x3.58mm, normal (0.67,0,-0.75), area 4.4mm2, adj f14,f23,f29
  f16: plane 11.91x5.62mm, normal (0,-1,0), area 52.3mm2, adj f2,f3,f13,f14,f18,f19,f28,f29
  f17: bspline ~23.11x23.11mm, area 0.4mm2, adj f18,f23,f42
  f18: bspline ~23.11x23.11mm, area 5.9mm2, adj f5,f14,f16,f17,f19,f42
  f19: plane 19.44x2.7mm, normal (0,-0.71,0.71), area 57.6mm2, adj f3,f4,f10,f11,f16,f18,f21,f42
  f20: plane 11.22x10.82mm, normal (-0.69,-0.72,0), area 84.7mm2, adj f10,f21,f27,f41
  f21: plane 12.24x11.9mm, normal (-0.49,-0.51,0.71), area 52.2mm2, adj f19,f20,f33,f42
  f22: plane 7.35x1.78mm, normal (0,1,0), area 13.1mm2, adj f23,f26,f38,f39
  f23: plane 10.5x8.78mm, normal (0.63,0.78,0), area 36.4mm2, adj f0,f5,f14,f15,f17,f22,f24,f30
  f24: cylinder r=3.43mm len=15.04mm, axis (-1,0,0), area 103.1mm2, adj f0,f6,f7,f8,f9,f23,f25,f38
  f25: torus R=6.37mm, axis (0,0,-1), area 136.6mm2, adj f0,f9,f24,f36,f38
  f26: cylinder r=4.73mm len=4.73mm, axis (0,0,-1), area 13.2mm2, adj f22,f37,f38,f39
  f27: plane 12.24x11.9mm, normal (-0.49,-0.51,-0.71), area 52.2mm2, adj f20,f28,f34,f40
  f28: plane 19.51x2.69mm, normal (0,-0.71,-0.71), area 57.4mm2, adj f10,f11,f12,f13,f16,f27,f29,f34
  f29: bspline ~23.11x23.11mm, area 5.5mm2, adj f14,f15,f16,f28,f30,f34
  f30: bspline ~23.11x23.11mm, area 0.2mm2, adj f23,f29,f31,f34
  f31: plane 10.8x0.02mm, normal (0,1,0), area 0.2mm2, adj f30,f32,f34,f39
  f32: cylinder r=6.37mm len=6.37mm, axis (0,0,-1), area 0.2mm2, adj f31,f34,f35,f39
  f33: plane 6.91x2.54mm, normal (-0.71,0,0.71), area 22.9mm2, adj f1,f21,f41,f42
  f34: plane 25.54x15.19mm, normal (0,0,-1), area 116.3mm2, adj f1,f27,f28,f29,f30,f31,f32,f35
  f35: plane 5.52x0.02mm, normal (1,0,0), area 0.1mm2, adj f1,f32,f34,f39
  f36: cylinder r=3.43mm len=6.85mm, axis (0,1,0), area 59.4mm2, adj f0,f1,f25,f38
  f37: plane 4.36x1.78mm, normal (1,0,0), area 7.8mm2, adj f1,f26,f38,f39
  f38: plane 17.17x11.89mm, normal (0,0,1), area 54.3mm2, adj f1,f22,f23,f24,f25,f26,f36,f37
  f39: plane 17.17x11.89mm, normal (0,0,-1), area 54.3mm2, adj f1,f22,f23,f26,f31,f32,f35,f37
  f40: plane 6.91x2.54mm, normal (-0.71,0,-0.71), area 22.9mm2, adj f1,f27,f34,f41
  f41: plane 6.91x5.44mm, normal (-1,0,0), area 37.5mm2, adj f1,f20,f33,f40
  f42: plane 25.59x15.28mm, normal (0,0,1), area 116.2mm2, adj f1,f17,f18,f19,f21,f33,f48
  f43: plane 4.28x1.87mm, normal (1,0,0), area 8mm2, adj f0,f1,f44,f47,f48
  f44: cylinder r=6.26mm len=6.26mm, axis (0,0,1), area 18.4mm2, adj f0,f43,f45,f48
  f45: plane 7.21x1.87mm, normal (0,1,0), area 13.5mm2, adj f0,f44,f46,f48
  f46: plane 1.87x1.85mm, normal (0,1,0), area 3.4mm2, adj f0,f23,f45,f48
  f47: bspline ~0.19x0.09mm, area 0mm2, adj f1,f43,f48
  f48: plane 17.18x11.9mm, normal (0,0,1), area 23.8mm2, adj f23,f42,f43,f44,f45,f46,f47
PLACE A rot(axis=(0,1,0),90deg) t=(20.57,5.11,38.7)mm
PLACE B rot(axis=(0,1,0),90deg) t=(20.57,19.08,38.7)mm
PLACE C rot(axis=(0,-1,0),90deg) t=(4.97,7.21,38.7)mm
PLACE D rot(axis=(0,-1,0),90deg) t=(4.97,21.18,38.7)mm
MATE fastened D.f1 <-> C.f2  axis (0,1,0) through (0.29,-33.73,4.09)mm
MATE fastened A.f52 <-> B.f44  axis (0,-1,0) through (25.24,-35.83,4.05)mm
